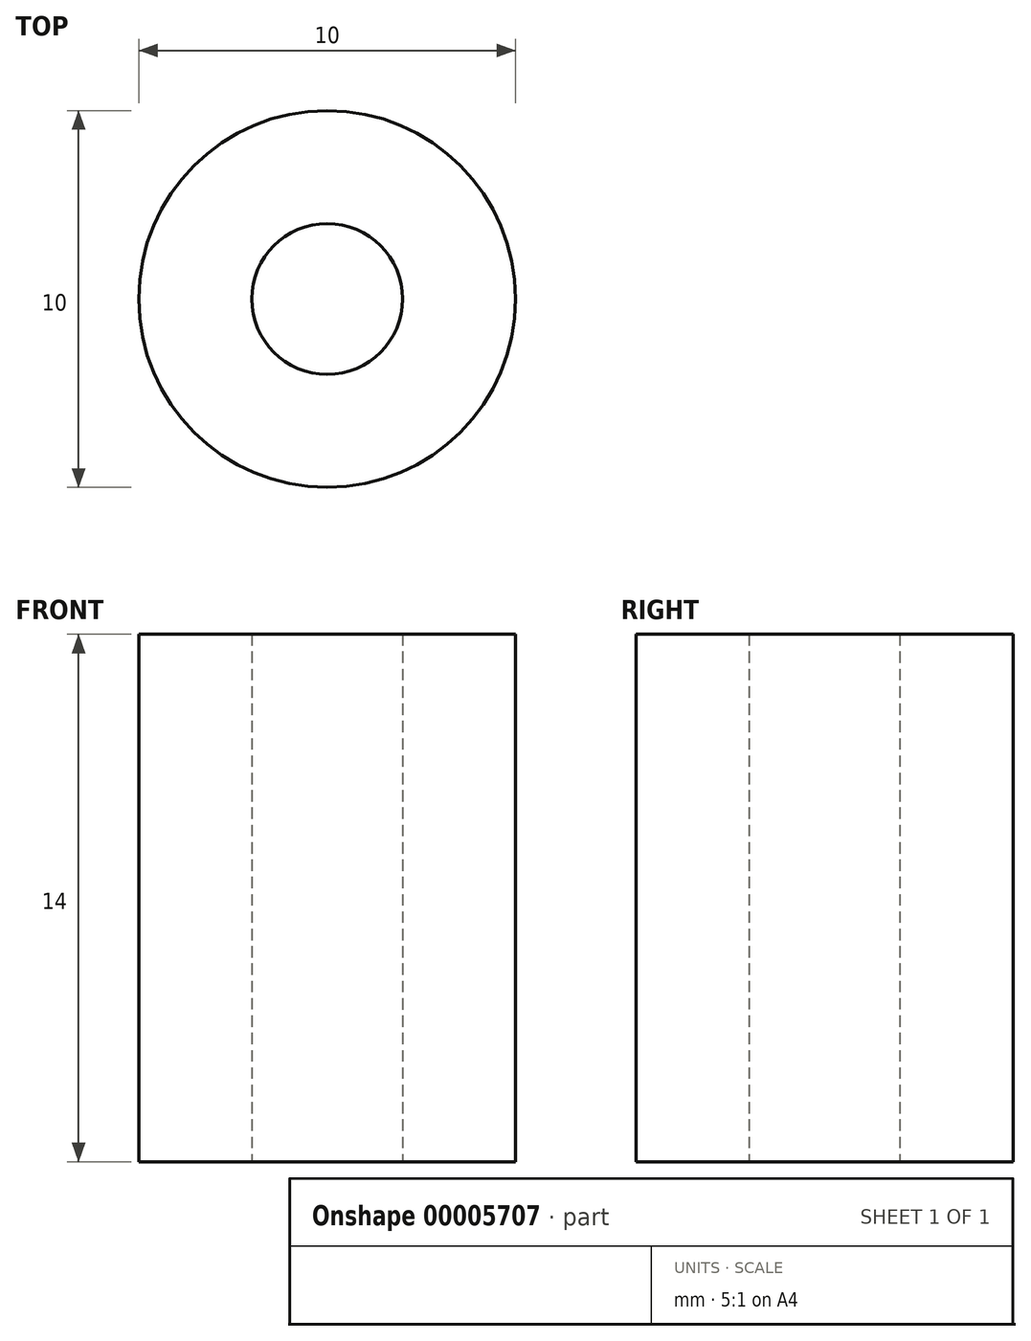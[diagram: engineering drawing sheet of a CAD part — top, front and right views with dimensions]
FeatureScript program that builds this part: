
annotation { "Feature Type Name" : "Feature", "Feature Type Description" : "" }
export const myFeature = defineFeature(function(context is Context, id is Id, definition is map)
    precondition{}
    {
        {
            var Q0;
            Q0=qCreatedBy(makeId("Top.planeOp"),FACE);
            var sketch = newSketch(context, id + "F0", { "sketchPlane" : qUnion([Q0])});
            skCircle(sketch, "E0", {"center": v(0, 0) * mm, "radius": 2 * mm});
            skCircle(sketch, "E1", {"center": v(0, 0) * mm, "radius": 5 * mm});
            skSolve(sketch);
        }
        {
            var Q0;
            Q0=makeQuery(id+"F0.imprint","IMPRINT",FACE,{"disambiguationData":[TD([[makeQuery(id+"F0.imprint","IMPRINT",EDGE,{"derivedFrom":sQuery(id+"F0.wireOp",EDGE,"E0")}),-1.0]])]});
            extrude(context, id + "F1", {"entities" : qUnion([Q0]), "depth" : 14 * mm});
        }
    });
